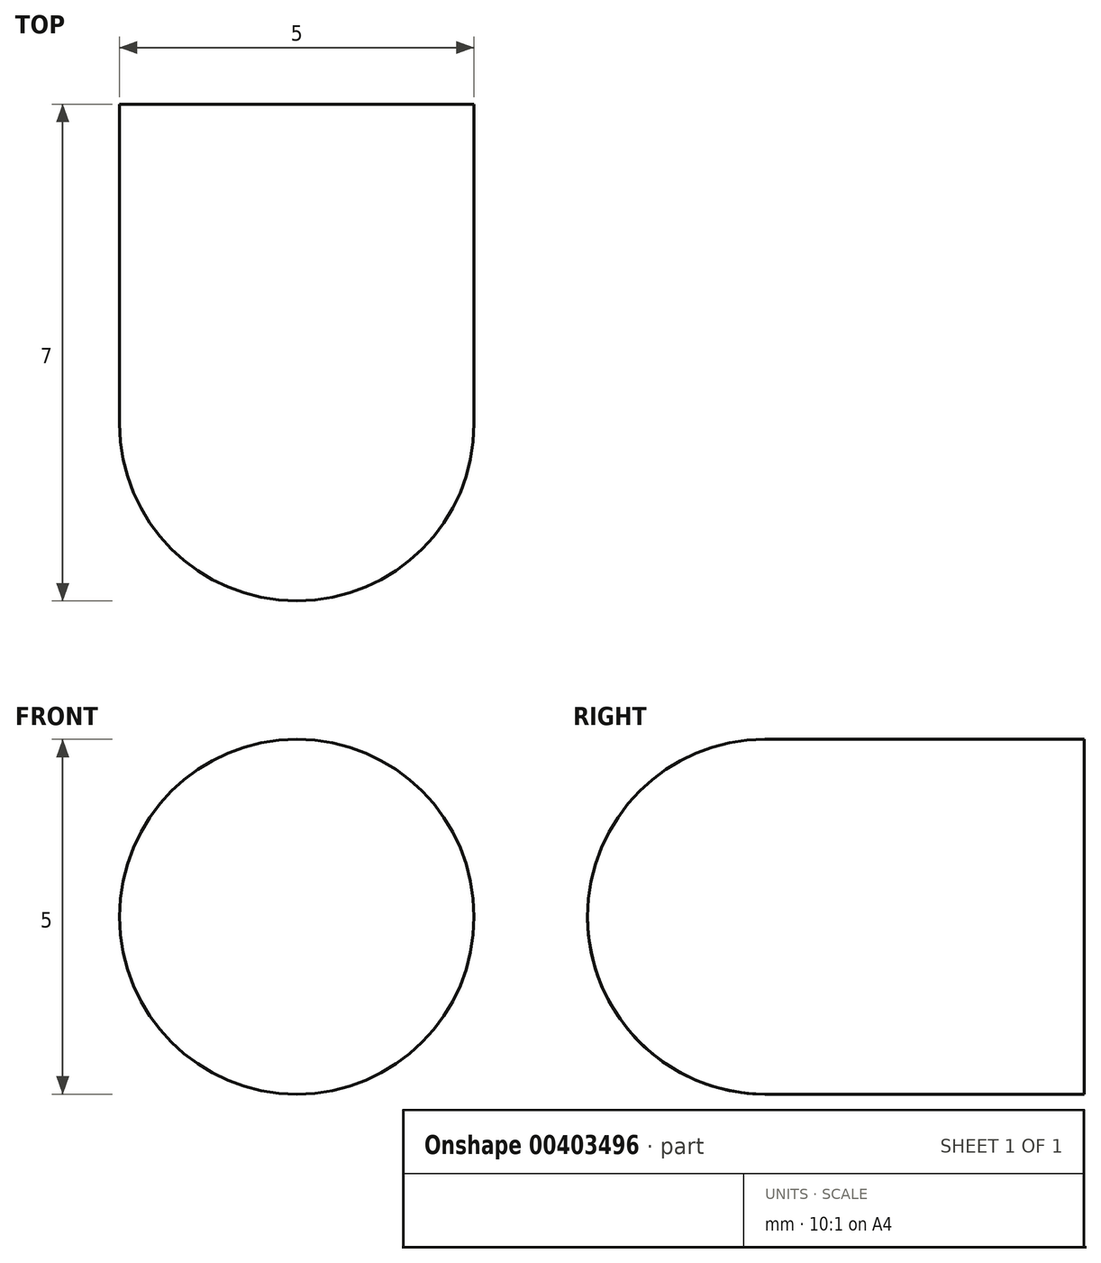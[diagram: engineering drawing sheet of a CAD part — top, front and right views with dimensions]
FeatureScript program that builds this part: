
annotation { "Feature Type Name" : "Feature", "Feature Type Description" : "" }
export const myFeature = defineFeature(function(context is Context, id is Id, definition is map)
    precondition{}
    {
        {
            var Q0;
            Q0=qCreatedBy(makeId("Front.planeOp"),FACE);
            var sketch = newSketch(context, id + "F0", { "sketchPlane" : qUnion([Q0])});
            skCircle(sketch, "E0", {"center": v(0, 0) * mm, "radius": 2.5 * mm});
            skSolve(sketch);
        }
        {
            var Q0;
            Q0=qSketchRegion(id+"F0",true);
            var Q1;
            Q1=makeQuery(id+"F0.imprint","IMPRINT",FACE,{"disambiguationData":[TD([[makeQuery(id+"F0.imprint","IMPRINT",EDGE,{"derivedFrom":sQuery(id+"F0.wireOp",EDGE,"E0")}),1.0]])]});
            extrude(context, id + "F1", {"entities" : qUnion([Q0, Q1]), "depth" : 7 * mm});
        }
        {
            var Q0;
            Q0=makeQuery(id+"F1.opExtrude","CAP_EDGE",EDGE,{"disambiguationData":[OSD([sQuery(id+"F0.wireOp",EDGE,"E0")])],"isStart":false});
            fillet(context, id + "F2", {"entities" : qUnion([Q0]), "radius" : 2.5 * mm, "tangentPropagation" : true, "allowEdgeOverflow" : false});
        }
    });
